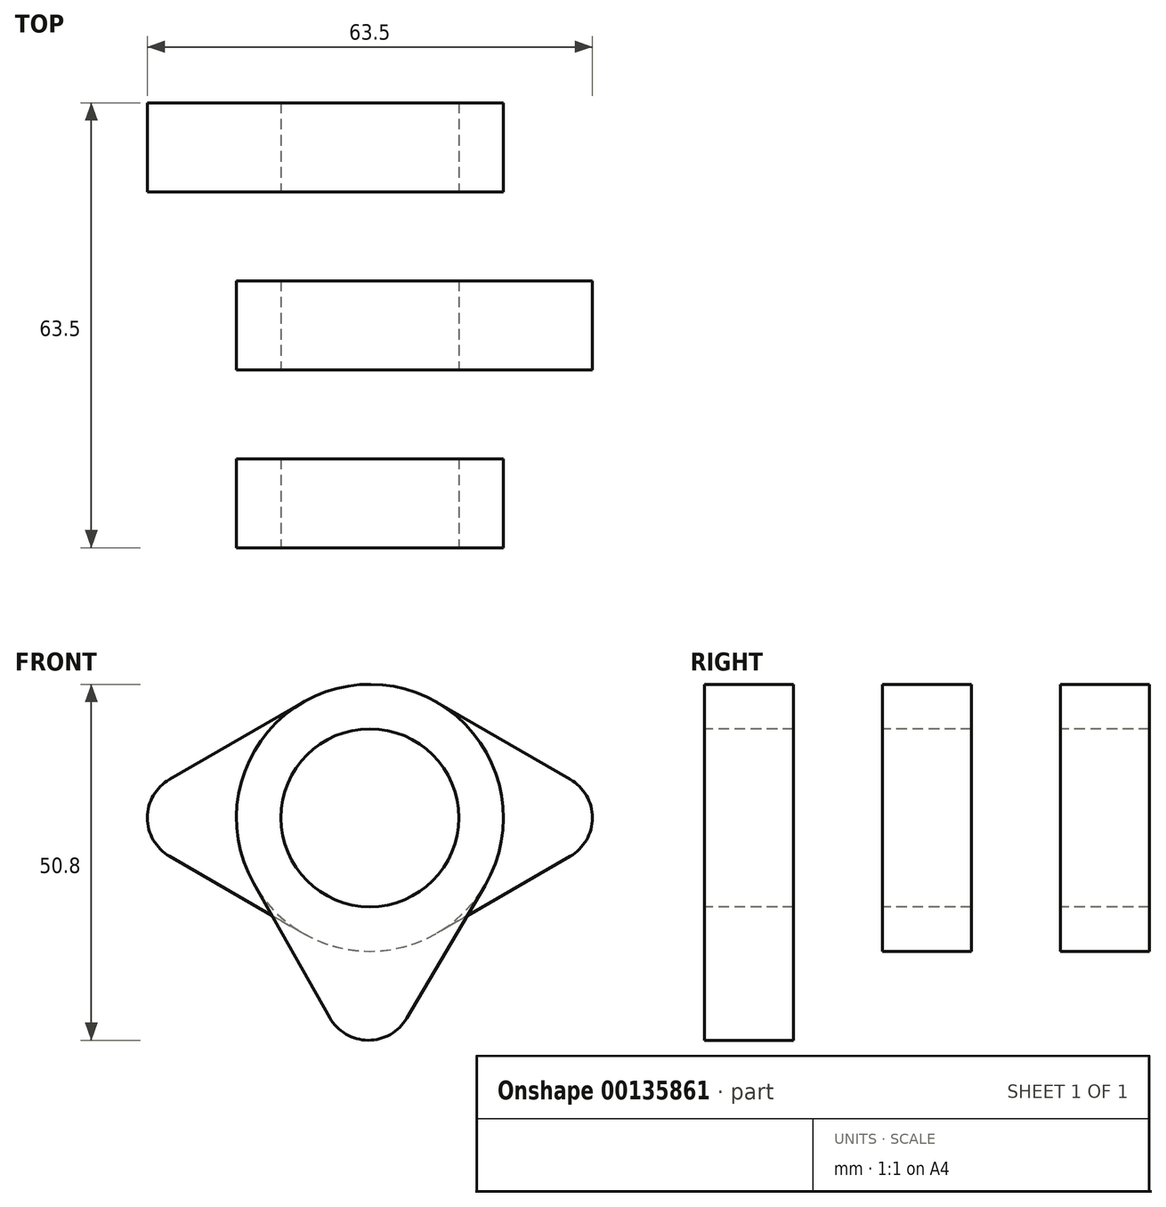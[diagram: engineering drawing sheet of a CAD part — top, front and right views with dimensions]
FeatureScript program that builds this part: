
annotation { "Feature Type Name" : "Feature", "Feature Type Description" : "" }
export const myFeature = defineFeature(function(context is Context, id is Id, definition is map)
    precondition{}
    {
        {
            var Q0;
            Q0=qCreatedBy(makeId("Front.planeOp"),FACE);
            var sketch = newSketch(context, id + "F0", { "sketchPlane" : qUnion([Q0])});
            skCircle(sketch, "E0", {"center": v(0, 0) * mm, "radius": 12.7 * mm});
            skArc(sketch, "E1", {"start": v(-5.73, -28.53) * mm, "mid": v(-0.26, -31.75) * mm, "end": v(5.27, -28.62) * mm});
            skArc(sketch, "E2", {"start": v(16.42, -9.66) * mm, "mid": v(0.15, 19.05) * mm, "end": v(-16.57, -9.4) * mm});
            skLineSegment(sketch, "E3", {"start": v(-5.73, -28.53) * mm, "end": v(-16.57, -9.4) * mm});
            skLineSegment(sketch, "E4", {"start": v(16.42, -9.66) * mm, "end": v(5.27, -28.62) * mm});
            skSolve(sketch);
        }
        {
            var Q0;
            Q0=makeQuery(id+"F0.imprint","IMPRINT",FACE,{"disambiguationData":[TD([[makeQuery(id+"F0.imprint","IMPRINT",EDGE,{"derivedFrom":sQuery(id+"F0.wireOp",EDGE,"E0")}),-1.0]])]});
            extrude(context, id + "F1", {"entities" : qUnion([Q0]), "oppositeDirection" : true, "depth" : 12.7 * mm});
        }
        {
            var Q0;
            Q0=makeQuery(id+"F1.opExtrude","CAP_FACE",FACE,{"disambiguationData":[OSD([sQuery(id+"F0.wireOp",EDGE,"E1"),sQuery(id+"F0.wireOp",EDGE,"E2"),sQuery(id+"F0.wireOp",EDGE,"E3"),sQuery(id+"F0.wireOp",EDGE,"E4")])],"isStart":true});
            cPlane(context, id + "F2", {"entities" : qUnion([Q0]), "cplaneType" : CPlaneType.OFFSET, "offset" : 25.4 * mm, "oppositeDirection" : true, "width" : 152.4 * mm, "height" : 152.4 * mm});
        }
        {
            var Q0;
            Q0=makeQuery(id+"F1.opExtrude","CAP_FACE",FACE,{"disambiguationData":[OSD([sQuery(id+"F0.wireOp",EDGE,"E1"),sQuery(id+"F0.wireOp",EDGE,"E2"),sQuery(id+"F0.wireOp",EDGE,"E3"),sQuery(id+"F0.wireOp",EDGE,"E4")])],"isStart":true});
            cPlane(context, id + "F3", {"entities" : qUnion([Q0]), "cplaneType" : CPlaneType.OFFSET, "offset" : 50.8 * mm, "oppositeDirection" : true, "width" : 152.4 * mm, "height" : 152.4 * mm});
        }
        {
            var Q0;
            Q0=qCreatedBy(id+"F2.planeOp",FACE);
            var sketch = newSketch(context, id + "F4", { "sketchPlane" : qUnion([Q0])});
            skCircle(sketch, "E5", {"center": v(0, 0) * mm, "radius": 12.7 * mm});
            skArc(sketch, "E6", {"start": v(9.52, 16.5) * mm, "mid": v(-19.05, 0) * mm, "end": v(9.52, -16.5) * mm});
            skLineSegment(sketch, "E7", {"start": v(0, 0) * mm, "end": v(25.4, 0) * mm});
            skArc(sketch, "E8", {"start": v(28.58, -5.5) * mm, "mid": v(31.75, 0) * mm, "end": v(28.58, 5.5) * mm});
            skLineSegment(sketch, "E9", {"start": v(28.58, 5.5) * mm, "end": v(9.52, 16.5) * mm});
            skLineSegment(sketch, "E10", {"start": v(28.58, -5.5) * mm, "end": v(9.53, -16.5) * mm});
            skSolve(sketch);
        }
        {
            var Q0;
            Q0=makeQuery(id+"F4.imprint","IMPRINT",FACE,{"disambiguationData":[TD([[makeQuery(id+"F4.imprint","IMPRINT",EDGE,{"derivedFrom":sQuery(id+"F4.wireOp",EDGE,"E5")}),-1.0]])]});
            extrude(context, id + "F5", {"entities" : qUnion([Q0]), "oppositeDirection" : true, "depth" : 12.7 * mm});
        }
        {
            var Q0;
            Q0=qCreatedBy(id+"F3.planeOp",FACE);
            var sketch = newSketch(context, id + "F6", { "sketchPlane" : qUnion([Q0])});
            skCircle(sketch, "E11", {"center": v(0, 0) * mm, "radius": 12.7 * mm});
            skArc(sketch, "E12", {"start": v(-9.53, -16.5) * mm, "mid": v(19.05, 0) * mm, "end": v(-9.52, 16.5) * mm});
            skLineSegment(sketch, "E13", {"start": v(0, 0) * mm, "end": v(-25.4, 0) * mm});
            skArc(sketch, "E14", {"start": v(-28.58, 5.5) * mm, "mid": v(-31.75, 0) * mm, "end": v(-28.58, -5.5) * mm});
            skLineSegment(sketch, "E15", {"start": v(-28.58, 5.5) * mm, "end": v(-9.52, 16.5) * mm});
            skLineSegment(sketch, "E16", {"start": v(-28.58, -5.5) * mm, "end": v(-9.53, -16.5) * mm});
            skSolve(sketch);
        }
        {
            var Q0;
            Q0 = qSketchRegion(id + "F6", true);
            var Q1;
            Q1=makeQuery(id+"F1.opExtrude","CAP_FACE",FACE,{"disambiguationData":[OSD([sQuery(id+"F0.wireOp",EDGE,"E0"),sQuery(id+"F0.wireOp",EDGE,"E1"),sQuery(id+"F0.wireOp",EDGE,"E2"),sQuery(id+"F0.wireOp",EDGE,"E3"),sQuery(id+"F0.wireOp",EDGE,"E4")])],"isStart":true});
            extrude(context, id + "F7", {"entities" : qUnion([Q0, Q1]), "operationType" : NewBodyOperationType.ADD, "oppositeDirection" : true, "depth" : 12.7 * mm});
        }
    });
